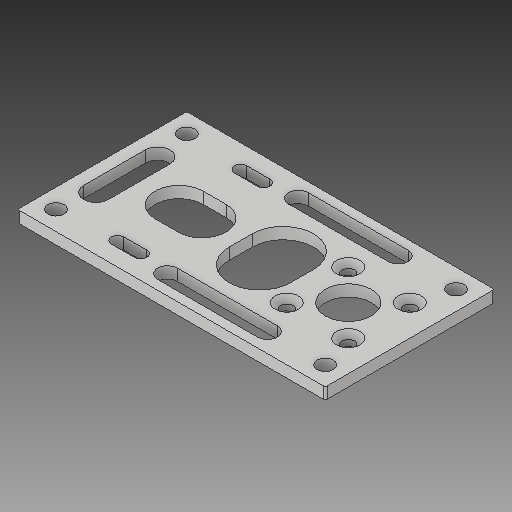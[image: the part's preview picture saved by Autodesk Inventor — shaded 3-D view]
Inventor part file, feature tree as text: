
AUTODESK INVENTOR PART (.ipt)
format: ipt  version: 2018 (Build 220112000, 112)  size: 181,248 bytes
history: native  units: in
note: dims shown in document units (in); Inventor stores cm internally (conversion verified against a paired STEP export)
features: fillet x1
ambient origin geometry x8: Origin, YZ Plane, XZ Plane, XY Plane, X Axis, Y Axis, Z Axis, Center Point
bodies: Solid1 (feature_tree)
feature tree (1):
  fillet  "Fillet1"  [1 undecoded]
note: 1 required parameter value undecoded (feature->parameter linkage not recoverable at this tier; creation-order binding heuristic only, values carry confidence <= 0.55)
